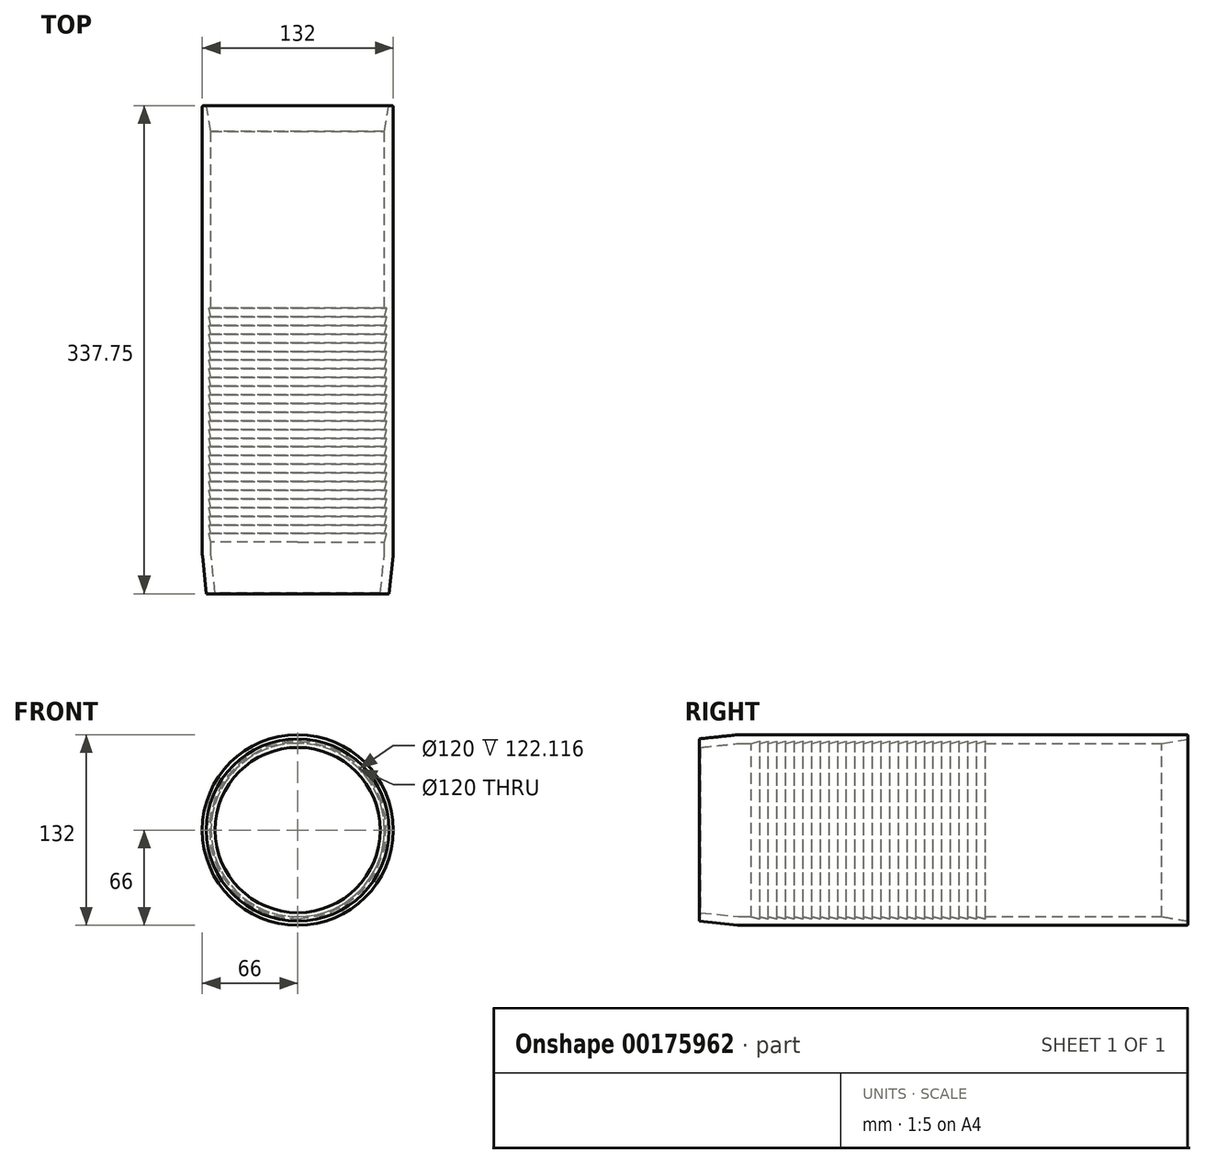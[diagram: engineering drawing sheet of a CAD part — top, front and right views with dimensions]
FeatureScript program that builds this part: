
annotation { "Feature Type Name" : "Feature", "Feature Type Description" : "" }
export const myFeature = defineFeature(function(context is Context, id is Id, definition is map)
    precondition{}
    {
        {
            var Q0;
            Q0=qCreatedBy(makeId("Right.planeOp"),FACE);
            var sketch = newSketch(context, id + "F0", { "sketchPlane" : qUnion([Q0])});
            skLineSegment(sketch, "E0", {"start": v(183.9, 0) * mm, "end": v(0, 0) * mm, "construction": true});
            skLineSegment(sketch, "E1", {"start": v(0, 57.15) * mm, "end": v(26.07, 59.9) * mm});
            skLineSegment(sketch, "E2", {"start": v(28.16, 60) * mm, "end": v(337.12, 60) * mm});
            skPoint(sketch, "E3.visualSharp", {"position": v(27.12, 60) * mm});
            skArc(sketch, "E3.filletArc", {"start": v(28.16, 60) * mm, "mid": v(27.12, 59.97) * mm, "end": v(26.07, 59.9) * mm});
            skLineSegment(sketch, "E4.0", {"start": v(28.16, 66) * mm, "end": v(337.12, 66) * mm});
            skArc(sketch, "E4.1", {"start": v(28.16, 66) * mm, "mid": v(26.8, 65.96) * mm, "end": v(25.45, 65.86) * mm});
            skLineSegment(sketch, "E4.2", {"start": v(-0.63, 63.12) * mm, "end": v(25.45, 65.86) * mm});
            skLineSegment(sketch, "E5", {"start": v(-0.63, 63.12) * mm, "end": v(0, 57.15) * mm});
            skLineSegment(sketch, "E6", {"start": v(337.12, 66) * mm, "end": v(337.12, 60) * mm});
            skSolve(sketch);
        }
        {
            var Q0;
            Q0 = qSketchRegion(id + "F0", true);
            var Q1;
            Q1=sQuery(id+"F0.wireOp",EDGE,"E0");
            revolve(context, id + "F1", {"entities" : qUnion([Q0]), "axis" : qUnion([Q1]), "revolveType" : RevolveType.FULL});
        }
        {
            var Q0;
            Q0=makeQuery(id+"F1.opRevolve","SWEPT_EDGE",EDGE,{"disambiguationData":[OSD([sQuery(id+"F0.wireOp",EDGE,"E2"),sQuery(id+"F0.wireOp",EDGE,"E6")])]});
            chamfer(context, id + "F2", {"entities" : qUnion([Q0]), "chamferType" : ChamferType.TWO_OFFSETS, "width1" : 18 * mm, "oppositeDirection" : false, "width2" : 3 * mm, "tangentPropagation" : true});
        }
        {
            var Q0;
            {var subQ0=sQuery(id+"F0.wireOp",EDGE,"E6");Q0=makeQuery(id+"F2.opChamfer","BLEND_EDGE",EDGE,{"blendedFrom":[makeQuery(id+"F1.opRevolve","SWEPT_EDGE",EDGE,{"disambiguationData":[OSD([sQuery(id+"F0.wireOp",EDGE,"E2"),subQ0])]}),makeQuery(id+"F1.opRevolve","SWEPT_FACE",FACE,{"disambiguationData":[OSD([subQ0])]})],"blendedInto":[makeQuery(id+"F1.opRevolve","SWEPT_FACE",FACE,{"disambiguationData":[OSD([subQ0])]})]});}
            var Q1;
            Q1=makeQuery(id+"F1.opRevolve","SWEPT_EDGE",EDGE,{"disambiguationData":[OSD([sQuery(id+"F0.wireOp",EDGE,"E4.0"),sQuery(id+"F0.wireOp",EDGE,"E6")])]});
            fillet(context, id + "F3", {"entities" : qUnion([Q0, Q1]), "radius" : 1 * mm, "tangentPropagation" : true, "allowEdgeOverflow" : false});
        }
        {
            var Q0;
            Q0=qCreatedBy(makeId("Right.planeOp"),FACE);
            var sketch = newSketch(context, id + "F4", { "sketchPlane" : qUnion([Q0])});
            skLineSegment(sketch, "E7", {"start": v(105.2, 0) * mm, "end": v(0, 0) * mm, "construction": true});
            skLineSegment(sketch, "E8", {"start": v(35, 60) * mm, "end": v(41, 60) * mm});
            skLineSegment(sketch, "E9", {"start": v(41, 60) * mm, "end": v(41, 61.24) * mm});
            skLineSegment(sketch, "E10", {"start": v(40.75, 61.44) * mm, "end": v(35, 60) * mm});
            skPoint(sketch, "E11.visualSharp", {"position": v(41, 61.5) * mm});
            skArc(sketch, "E11.filletArc", {"start": v(41, 61.24) * mm, "mid": v(40.92, 61.4) * mm, "end": v(40.75, 61.44) * mm});
            skLineSegment(sketch, "E12.1.0.0", {"start": v(41, 60) * mm, "end": v(47, 60) * mm});
            skArc(sketch, "E12.1.0.1", {"start": v(47, 61.24) * mm, "mid": v(46.92, 61.4) * mm, "end": v(46.75, 61.44) * mm});
            skLineSegment(sketch, "E12.1.0.2", {"start": v(47, 60) * mm, "end": v(47, 61.24) * mm});
            skLineSegment(sketch, "E12.1.0.3", {"start": v(46.75, 61.44) * mm, "end": v(41, 60) * mm});
            skLineSegment(sketch, "E12.2.0.0", {"start": v(47, 60) * mm, "end": v(53, 60) * mm});
            skArc(sketch, "E12.2.0.1", {"start": v(53, 61.24) * mm, "mid": v(52.92, 61.4) * mm, "end": v(52.75, 61.44) * mm});
            skLineSegment(sketch, "E12.2.0.2", {"start": v(53, 60) * mm, "end": v(53, 61.24) * mm});
            skLineSegment(sketch, "E12.2.0.3", {"start": v(52.75, 61.44) * mm, "end": v(47, 60) * mm});
            skLineSegment(sketch, "E12.direction1", {"start": v(35, 60) * mm, "end": v(41, 60) * mm, "construction": true});
            skLineSegment(sketch, "E13.0.3.0", {"start": v(53, 60) * mm, "end": v(59, 60) * mm});
            skArc(sketch, "E13.3.3.0", {"start": v(59, 61.24) * mm, "mid": v(58.92, 61.4) * mm, "end": v(58.75, 61.44) * mm});
            skLineSegment(sketch, "E13.7.3.0", {"start": v(59, 60) * mm, "end": v(59, 61.24) * mm});
            skLineSegment(sketch, "E13.10.3.0", {"start": v(58.75, 61.44) * mm, "end": v(53, 60) * mm});
            skLineSegment(sketch, "E13.0.4.0", {"start": v(59, 60) * mm, "end": v(65, 60) * mm});
            skArc(sketch, "E13.3.4.0", {"start": v(65, 61.24) * mm, "mid": v(64.92, 61.4) * mm, "end": v(64.75, 61.44) * mm});
            skLineSegment(sketch, "E13.7.4.0", {"start": v(65, 60) * mm, "end": v(65, 61.24) * mm});
            skLineSegment(sketch, "E13.10.4.0", {"start": v(64.75, 61.44) * mm, "end": v(59, 60) * mm});
            skLineSegment(sketch, "E13.0.5.0", {"start": v(65, 60) * mm, "end": v(71, 60) * mm});
            skArc(sketch, "E13.3.5.0", {"start": v(71, 61.24) * mm, "mid": v(70.92, 61.4) * mm, "end": v(70.75, 61.44) * mm});
            skLineSegment(sketch, "E13.7.5.0", {"start": v(71, 60) * mm, "end": v(71, 61.24) * mm});
            skLineSegment(sketch, "E13.10.5.0", {"start": v(70.75, 61.44) * mm, "end": v(65, 60) * mm});
            skLineSegment(sketch, "E13.0.6.0", {"start": v(71, 60) * mm, "end": v(77, 60) * mm});
            skArc(sketch, "E13.3.6.0", {"start": v(77, 61.24) * mm, "mid": v(76.92, 61.4) * mm, "end": v(76.75, 61.44) * mm});
            skLineSegment(sketch, "E13.7.6.0", {"start": v(77, 60) * mm, "end": v(77, 61.24) * mm});
            skLineSegment(sketch, "E13.10.6.0", {"start": v(76.75, 61.44) * mm, "end": v(71, 60) * mm});
            skLineSegment(sketch, "E13.0.7.0", {"start": v(77, 60) * mm, "end": v(83, 60) * mm});
            skArc(sketch, "E13.3.7.0", {"start": v(83, 61.24) * mm, "mid": v(82.92, 61.4) * mm, "end": v(82.75, 61.44) * mm});
            skLineSegment(sketch, "E13.7.7.0", {"start": v(83, 60) * mm, "end": v(83, 61.24) * mm});
            skLineSegment(sketch, "E13.10.7.0", {"start": v(82.75, 61.44) * mm, "end": v(77, 60) * mm});
            skLineSegment(sketch, "E13.0.8.0", {"start": v(83, 60) * mm, "end": v(89, 60) * mm});
            skArc(sketch, "E13.3.8.0", {"start": v(89, 61.24) * mm, "mid": v(88.92, 61.4) * mm, "end": v(88.75, 61.44) * mm});
            skLineSegment(sketch, "E13.7.8.0", {"start": v(89, 60) * mm, "end": v(89, 61.24) * mm});
            skLineSegment(sketch, "E13.10.8.0", {"start": v(88.75, 61.44) * mm, "end": v(83, 60) * mm});
            skLineSegment(sketch, "E13.0.9.0", {"start": v(89, 60) * mm, "end": v(95, 60) * mm});
            skArc(sketch, "E13.3.9.0", {"start": v(95, 61.24) * mm, "mid": v(94.92, 61.4) * mm, "end": v(94.75, 61.44) * mm});
            skLineSegment(sketch, "E13.7.9.0", {"start": v(95, 60) * mm, "end": v(95, 61.24) * mm});
            skLineSegment(sketch, "E13.10.9.0", {"start": v(94.75, 61.44) * mm, "end": v(89, 60) * mm});
            skLineSegment(sketch, "E13.0.10.0", {"start": v(95, 60) * mm, "end": v(101, 60) * mm});
            skArc(sketch, "E13.3.10.0", {"start": v(101, 61.24) * mm, "mid": v(100.92, 61.4) * mm, "end": v(100.75, 61.44) * mm});
            skLineSegment(sketch, "E13.7.10.0", {"start": v(101, 60) * mm, "end": v(101, 61.24) * mm});
            skLineSegment(sketch, "E13.10.10.0", {"start": v(100.75, 61.44) * mm, "end": v(95, 60) * mm});
            skLineSegment(sketch, "E13.0.11.0", {"start": v(101, 60) * mm, "end": v(107, 60) * mm});
            skArc(sketch, "E13.3.11.0", {"start": v(107, 61.24) * mm, "mid": v(106.92, 61.4) * mm, "end": v(106.75, 61.44) * mm});
            skLineSegment(sketch, "E13.7.11.0", {"start": v(107, 60) * mm, "end": v(107, 61.24) * mm});
            skLineSegment(sketch, "E13.10.11.0", {"start": v(106.75, 61.44) * mm, "end": v(101, 60) * mm});
            skLineSegment(sketch, "E13.0.12.0", {"start": v(107, 60) * mm, "end": v(113, 60) * mm});
            skArc(sketch, "E13.3.12.0", {"start": v(113, 61.24) * mm, "mid": v(112.92, 61.4) * mm, "end": v(112.75, 61.44) * mm});
            skLineSegment(sketch, "E13.7.12.0", {"start": v(113, 60) * mm, "end": v(113, 61.24) * mm});
            skLineSegment(sketch, "E13.10.12.0", {"start": v(112.75, 61.44) * mm, "end": v(107, 60) * mm});
            skLineSegment(sketch, "E13.0.13.0", {"start": v(113, 60) * mm, "end": v(119, 60) * mm});
            skArc(sketch, "E13.3.13.0", {"start": v(119, 61.24) * mm, "mid": v(118.92, 61.4) * mm, "end": v(118.75, 61.44) * mm});
            skLineSegment(sketch, "E13.7.13.0", {"start": v(119, 60) * mm, "end": v(119, 61.24) * mm});
            skLineSegment(sketch, "E13.10.13.0", {"start": v(118.75, 61.44) * mm, "end": v(113, 60) * mm});
            skLineSegment(sketch, "E13.0.14.0", {"start": v(119, 60) * mm, "end": v(125, 60) * mm});
            skArc(sketch, "E13.3.14.0", {"start": v(125, 61.24) * mm, "mid": v(124.92, 61.4) * mm, "end": v(124.75, 61.44) * mm});
            skLineSegment(sketch, "E13.7.14.0", {"start": v(125, 60) * mm, "end": v(125, 61.24) * mm});
            skLineSegment(sketch, "E13.10.14.0", {"start": v(124.75, 61.44) * mm, "end": v(119, 60) * mm});
            skLineSegment(sketch, "E13.0.15.0", {"start": v(125, 60) * mm, "end": v(131, 60) * mm});
            skArc(sketch, "E13.3.15.0", {"start": v(131, 61.24) * mm, "mid": v(130.92, 61.4) * mm, "end": v(130.75, 61.44) * mm});
            skLineSegment(sketch, "E13.7.15.0", {"start": v(131, 60) * mm, "end": v(131, 61.24) * mm});
            skLineSegment(sketch, "E13.10.15.0", {"start": v(130.75, 61.44) * mm, "end": v(125, 60) * mm});
            skLineSegment(sketch, "E13.0.16.0", {"start": v(131, 60) * mm, "end": v(137, 60) * mm});
            skArc(sketch, "E13.3.16.0", {"start": v(137, 61.24) * mm, "mid": v(136.92, 61.4) * mm, "end": v(136.75, 61.44) * mm});
            skLineSegment(sketch, "E13.7.16.0", {"start": v(137, 60) * mm, "end": v(137, 61.24) * mm});
            skLineSegment(sketch, "E13.10.16.0", {"start": v(136.75, 61.44) * mm, "end": v(131, 60) * mm});
            skLineSegment(sketch, "E13.0.17.0", {"start": v(137, 60) * mm, "end": v(143, 60) * mm});
            skArc(sketch, "E13.3.17.0", {"start": v(143, 61.24) * mm, "mid": v(142.92, 61.4) * mm, "end": v(142.75, 61.44) * mm});
            skLineSegment(sketch, "E13.7.17.0", {"start": v(143, 60) * mm, "end": v(143, 61.24) * mm});
            skLineSegment(sketch, "E13.10.17.0", {"start": v(142.75, 61.44) * mm, "end": v(137, 60) * mm});
            skLineSegment(sketch, "E13.0.18.0", {"start": v(143, 60) * mm, "end": v(149, 60) * mm});
            skArc(sketch, "E13.3.18.0", {"start": v(149, 61.24) * mm, "mid": v(148.92, 61.4) * mm, "end": v(148.75, 61.44) * mm});
            skLineSegment(sketch, "E13.7.18.0", {"start": v(149, 60) * mm, "end": v(149, 61.24) * mm});
            skLineSegment(sketch, "E13.10.18.0", {"start": v(148.75, 61.44) * mm, "end": v(143, 60) * mm});
            skLineSegment(sketch, "E13.0.19.0", {"start": v(149, 60) * mm, "end": v(155, 60) * mm});
            skArc(sketch, "E13.3.19.0", {"start": v(155, 61.24) * mm, "mid": v(154.92, 61.4) * mm, "end": v(154.75, 61.44) * mm});
            skLineSegment(sketch, "E13.7.19.0", {"start": v(155, 60) * mm, "end": v(155, 61.24) * mm});
            skLineSegment(sketch, "E13.10.19.0", {"start": v(154.75, 61.44) * mm, "end": v(149, 60) * mm});
            skLineSegment(sketch, "E13.0.20.0", {"start": v(155, 60) * mm, "end": v(161, 60) * mm});
            skArc(sketch, "E13.3.20.0", {"start": v(161, 61.24) * mm, "mid": v(160.92, 61.4) * mm, "end": v(160.75, 61.44) * mm});
            skLineSegment(sketch, "E13.7.20.0", {"start": v(161, 60) * mm, "end": v(161, 61.24) * mm});
            skLineSegment(sketch, "E13.10.20.0", {"start": v(160.75, 61.44) * mm, "end": v(155, 60) * mm});
            skLineSegment(sketch, "E13.0.21.0", {"start": v(161, 60) * mm, "end": v(167, 60) * mm});
            skArc(sketch, "E13.3.21.0", {"start": v(167, 61.24) * mm, "mid": v(166.92, 61.4) * mm, "end": v(166.75, 61.44) * mm});
            skLineSegment(sketch, "E13.7.21.0", {"start": v(167, 60) * mm, "end": v(167, 61.24) * mm});
            skLineSegment(sketch, "E13.10.21.0", {"start": v(166.75, 61.44) * mm, "end": v(161, 60) * mm});
            skLineSegment(sketch, "E13.0.22.0", {"start": v(167, 60) * mm, "end": v(173, 60) * mm});
            skArc(sketch, "E13.3.22.0", {"start": v(173, 61.24) * mm, "mid": v(172.92, 61.4) * mm, "end": v(172.75, 61.44) * mm});
            skLineSegment(sketch, "E13.7.22.0", {"start": v(173, 60) * mm, "end": v(173, 61.24) * mm});
            skLineSegment(sketch, "E13.10.22.0", {"start": v(172.75, 61.44) * mm, "end": v(167, 60) * mm});
            skLineSegment(sketch, "E13.0.23.0", {"start": v(173, 60) * mm, "end": v(179, 60) * mm});
            skArc(sketch, "E13.3.23.0", {"start": v(179, 61.24) * mm, "mid": v(178.92, 61.4) * mm, "end": v(178.75, 61.44) * mm});
            skLineSegment(sketch, "E13.7.23.0", {"start": v(179, 60) * mm, "end": v(179, 61.24) * mm});
            skLineSegment(sketch, "E13.10.23.0", {"start": v(178.75, 61.44) * mm, "end": v(173, 60) * mm});
            skLineSegment(sketch, "E13.0.24.0", {"start": v(179, 60) * mm, "end": v(185, 60) * mm});
            skArc(sketch, "E13.3.24.0", {"start": v(185, 61.24) * mm, "mid": v(184.92, 61.4) * mm, "end": v(184.75, 61.44) * mm});
            skLineSegment(sketch, "E13.7.24.0", {"start": v(185, 60) * mm, "end": v(185, 61.24) * mm});
            skLineSegment(sketch, "E13.10.24.0", {"start": v(184.75, 61.44) * mm, "end": v(179, 60) * mm});
            skLineSegment(sketch, "E13.0.25.0", {"start": v(185, 60) * mm, "end": v(191, 60) * mm});
            skArc(sketch, "E13.3.25.0", {"start": v(191, 61.24) * mm, "mid": v(190.92, 61.4) * mm, "end": v(190.75, 61.44) * mm});
            skLineSegment(sketch, "E13.7.25.0", {"start": v(191, 60) * mm, "end": v(191, 61.24) * mm});
            skLineSegment(sketch, "E13.10.25.0", {"start": v(190.75, 61.44) * mm, "end": v(185, 60) * mm});
            skLineSegment(sketch, "E13.0.26.0", {"start": v(191, 60) * mm, "end": v(197, 60) * mm});
            skArc(sketch, "E13.3.26.0", {"start": v(197, 61.24) * mm, "mid": v(196.92, 61.4) * mm, "end": v(196.75, 61.44) * mm});
            skLineSegment(sketch, "E13.7.26.0", {"start": v(197, 60) * mm, "end": v(197, 61.24) * mm});
            skLineSegment(sketch, "E13.10.26.0", {"start": v(196.75, 61.44) * mm, "end": v(191, 60) * mm});
            skSolve(sketch);
        }
        {
            var Q0;
            Q0 = qSketchRegion(id + "F4", true);
            var Q1;
            Q1=sQuery(id+"F4.wireOp",EDGE,"E7");
            revolve(context, id + "F5", {"operationType" : NewBodyOperationType.REMOVE, "entities" : qUnion([Q0]), "axis" : qUnion([Q1]), "revolveType" : RevolveType.FULL, "oppositeDirection" : true});
        }
    });
